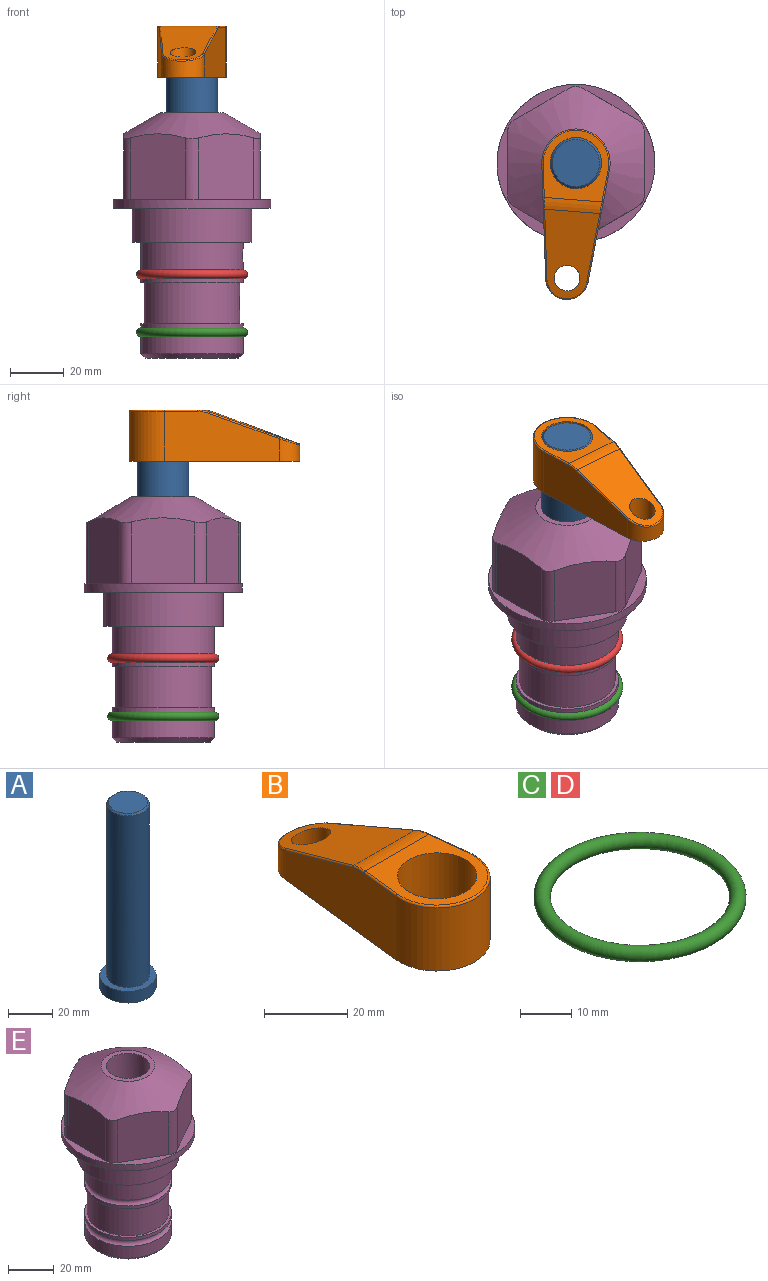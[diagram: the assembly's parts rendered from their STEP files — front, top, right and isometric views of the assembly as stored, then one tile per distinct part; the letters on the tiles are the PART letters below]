
ASSEMBLY  parts=5 mates=3
PART A: 6 faces, bbox 25.4x25.4x101.6 mm
  f0: plane 17.46x17.46mm, normal (0,0,1), area 239.5mm2, adj f5
  f1: plane 25.4x25.4mm, normal (0,0,-1), area 506.7mm2, adj f2
  f2: cylinder r=12.7mm len=25.4mm, axis (0,0,1), area 506.7mm2, adj f1,f3
  f3: plane 25.4x25.4mm, normal (0,0,1), area 221.7mm2, adj f2,f4
  f4: cylinder r=9.53mm len=94.46mm, axis (0,0,1), area 5653mm2, adj f3,f5
  f5: cone r=8.73mm half-angle=45deg, axis (0,0,-1), area 64.4mm2, adj f0,f4
PART B: 44 faces, bbox 27.5x64.5x19.1 mm
  f0: plane 2.3x0.95mm, normal (0,0,-1), area 1mm2, adj f25,f30,f34
  f1: plane 63.5x25.4mm, normal (0,0,-1), area 561.7mm2, adj f2,f3,f4,f5,f6,f7,f19,f20
  f2: cylinder r=12.7mm len=25.4mm, axis (0,0,-1), area 792.2mm2, adj f1,f3,f5,f13
  f3: plane 42.33x18.54mm, normal (0.99,0.11,0), area 647mm2, adj f1,f2,f4,f11,f12,f14
  f4: cylinder r=7.94mm len=15.78mm, axis (0,0,-1), area 158.6mm2, adj f1,f3,f5,f16
  f5: plane 42.33x18.54mm, normal (-0.99,0.11,0), area 647mm2, adj f1,f2,f4,f15,f17,f18
  f6: cylinder r=9.53mm len=19.05mm, axis (0,0,-1), area 1140.1mm2, adj f1,f8
  f7: cylinder r=4.76mm len=10.98mm, axis (0,0,-1), area 276.1mm2, adj f1,f9
  f8: plane 25.83x24.38mm, normal (0,0,1), area 262.2mm2, adj f6,f10,f11,f13,f15
  f9: plane 32.49x20.55mm, normal (0,0.34,0.94), area 489.9mm2, adj f7,f10,f14,f16,f18
  f10: cylinder r=12.7mm len=21.49mm, axis (-1,0,0), area 93.2mm2, adj f8,f9,f12,f17
  f11: cylinder r=0.51mm len=12.34mm, axis (0.11,-0.99,0), area 9.9mm2, adj f3,f8,f12,f13
  f12: bspline ~7.62x1.64mm, area 3.5mm2, adj f3,f10,f11,f14
  f13: torus R=12.19mm, axis (0,0,1), area 33.6mm2, adj f2,f8,f11,f15
  f14: cylinder r=0.51mm len=26.01mm, axis (0.1,-0.93,0.34), area 21.6mm2, adj f3,f9,f12,f16
  f15: cylinder r=0.51mm len=12.34mm, axis (0.11,0.99,0), area 9.9mm2, adj f5,f8,f13,f17
  f16: bspline ~15.78x7.05mm, area 15.7mm2, adj f4,f9,f14,f18
  f17: bspline ~7.62x1.64mm, area 3.5mm2, adj f5,f10,f15,f18
  f18: cylinder r=0.51mm len=26.01mm, axis (0.1,0.93,-0.34), area 21.6mm2, adj f5,f9,f16,f17
  f19: plane 21.6x14.29mm, normal (-0.99,-0.11,0), area 242.6mm2, adj f1,f26,f28,f34,f36,f38
  f20: plane 21.6x14.29mm, normal (0.99,-0.11,0), area 242.6mm2, adj f1,f27,f29,f37,f39,f41
  f21: cylinder r=12.7mm len=14.29mm, axis (0,0,-1), area 173.2mm2, adj f1,f26,f27,f30,f31,f33
  f22: cylinder r=7.94mm len=7.63mm, axis (0,0,-1), area 53.8mm2, adj f1,f28,f29,f42
  f23: plane 2.3x0.95mm, normal (0,0,-1), area 1mm2, adj f25,f33,f37
  f24: plane 17.94x12.32mm, normal (0,-0.34,-0.94), area 191.2mm2, adj f25,f38,f41,f42
  f25: cylinder r=9.53mm len=12.93mm, axis (-1,0,0), area 37.5mm2, adj f0,f23,f24,f31,f36,f39
  f26: cylinder r=1.59mm len=14.29mm, axis (0,0,-1), area 49mm2, adj f1,f19,f21,f32
  f27: cylinder r=1.59mm len=14.29mm, axis (0,0,-1), area 49mm2, adj f1,f20,f21,f35
  f28: cylinder r=1.59mm len=7.28mm, axis (0,0,-1), area 22.1mm2, adj f1,f19,f22,f40
  f29: cylinder r=1.59mm len=7.28mm, axis (0,0,-1), area 22.1mm2, adj f1,f20,f22,f43
  f30: torus R=14.29mm, axis (0,0,1), area 5.8mm2, adj f0,f21,f31,f32
  f31: bspline ~11.06x2.73mm, area 20.8mm2, adj f21,f25,f30,f33
  f32: sphere r=1.59mm, area 5.4mm2, adj f26,f30,f34
  f33: torus R=14.29mm, axis (0,0,1), area 5.8mm2, adj f21,f23,f31,f35
  f34: cylinder r=1.59mm len=1.68mm, axis (-0.11,0.99,0), area 2.4mm2, adj f0,f19,f32,f36
  f35: sphere r=1.59mm, area 5.4mm2, adj f27,f33,f37
  f36: bspline ~5.82x2.33mm, area 7.7mm2, adj f19,f25,f34,f38
  f37: cylinder r=1.59mm len=1.68mm, axis (0.11,0.99,0), area 2.4mm2, adj f20,f23,f35,f39
  f38: cylinder r=1.59mm len=18.33mm, axis (0.1,-0.93,0.34), area 46.7mm2, adj f19,f24,f36,f40
  f39: bspline ~5.82x2.33mm, area 7.7mm2, adj f20,f25,f37,f41
  f40: sphere r=1.59mm, area 3.6mm2, adj f28,f38,f42
  f41: cylinder r=1.59mm len=18.33mm, axis (0.1,0.93,-0.34), area 46.7mm2, adj f20,f24,f39,f43
  f42: bspline ~8.31x1.84mm, area 15.3mm2, adj f22,f24,f40,f43
  f43: sphere r=1.59mm, area 3.6mm2, adj f29,f41,f42
PART C: 1 faces, bbox 44.7x44.7x3.2 mm
  f0: torus R=19.05mm, axis (0,0,1), area 1193.9mm2
PART D: same geometry as C
PART E: 36 faces, bbox 58.7x58.7x91.2 mm
  f0: cylinder r=17.78mm len=35.56mm, axis (0,0,1), area 1670.8mm2, adj f23,f24,f31
  f1: cylinder r=19.05mm len=38.1mm, axis (0,0,1), area 1191.9mm2, adj f26,f27,f30
  f2: plane 58.66x58.66mm, normal (0,0,-1), area 1150.6mm2, adj f3,f28
  f3: cylinder r=29.33mm len=58.66mm, axis (0,0,-1), area 585.1mm2, adj f2,f4
  f4: plane 58.66x58.66mm, normal (0,0,1), area 475.9mm2, adj f3,f5,f6,f7,f8,f9,f10,f11
  f5: plane 24.5x20.32mm, normal (-0.5,0.87,0), area 562.8mm2, adj f4,f15,f16,f17
  f6: plane 24.5x20.32mm, normal (0.5,0.87,0), area 562.8mm2, adj f4,f14,f15,f17
  f7: plane 24.5x23.48mm, normal (1,0,0), area 562.8mm2, adj f4,f13,f14,f17
  f8: plane 24.5x20.32mm, normal (0.5,-0.87,0), area 562.8mm2, adj f4,f12,f13,f17
  f9: plane 24.5x20.32mm, normal (-0.5,-0.87,0), area 562.8mm2, adj f4,f11,f12,f17
  f10: plane 24.5x23.48mm, normal (-1,0,0), area 562.8mm2, adj f4,f11,f16,f17
  f11: cylinder r=5.08mm len=23.01mm, axis (0,0,-1), area 121.2mm2, adj f4,f9,f10,f17
  f12: cylinder r=5.08mm len=23.01mm, axis (0,0,-1), area 121.2mm2, adj f4,f8,f9,f17
  f13: cylinder r=5.08mm len=23.01mm, axis (0,0,-1), area 121.2mm2, adj f4,f7,f8,f17
  f14: cylinder r=5.08mm len=23.01mm, axis (0,0,-1), area 121.2mm2, adj f4,f6,f7,f17
  f15: cylinder r=5.08mm len=23.01mm, axis (0,0,-1), area 121.2mm2, adj f4,f5,f6,f17
  f16: cylinder r=5.08mm len=23.01mm, axis (0,0,-1), area 121.2mm2, adj f4,f5,f10,f17
  f17: cone r=11.73mm half-angle=60deg, axis (0,0,-1), area 2071.8mm2, adj f5,f6,f7,f8,f9,f10,f11,f12
  f18: plane 23.46x23.46mm, normal (0,0,1), area 147.4mm2, adj f17,f35
  f19: plane 34.93x34.93mm, normal (0,0,-1), area 958mm2, adj f29
  f20: cylinder r=19.05mm len=38.1mm, axis (0,0,1), area 760.1mm2, adj f21,f29
  f21: torus R=19.05mm, axis (0,0,1), area 565.3mm2, adj f20,f22
  f22: cylinder r=19.05mm len=38.1mm, axis (0,0,1), area 190mm2, adj f21,f23
  f23: plane 38.1x38.1mm, normal (0,0,1), area 146.9mm2, adj f0,f22
  f24: plane 38.1x38.1mm, normal (0,0,-1), area 146.9mm2, adj f0,f25
  f25: cylinder r=19.05mm len=38.1mm, axis (0,0,1), area 190mm2, adj f24,f26
  f26: torus R=19.05mm, axis (0,0,1), area 565.3mm2, adj f1,f25
  f27: plane 44.45x44.45mm, normal (0,0,-1), area 411.7mm2, adj f1,f28
  f28: cylinder r=22.23mm len=44.45mm, axis (0,0,1), area 1773.5mm2, adj f2,f27
  f29: cone r=19.05mm half-angle=45deg, axis (0,0,1), area 257.5mm2, adj f19,f20
  f30: cylinder r=3.17mm len=6.75mm, axis (-1,0,0), area 128mm2, adj f1,f33
  f31: cylinder r=3.17mm len=6.35mm, axis (-1,0,0), area 102.5mm2, adj f0,f33
  f32: plane 25.4x25.4mm, normal (0,0,1), area 506.7mm2, adj f33
  f33: cylinder r=12.7mm len=66.42mm, axis (0,0,-1), area 5236.2mm2, adj f30,f31,f32,f34
  f34: cone r=9.53mm half-angle=30deg, axis (0,0,-1), area 443.4mm2, adj f33,f35
  f35: cylinder r=9.53mm len=19.05mm, axis (0,0,-1), area 849mm2, adj f18,f34
PLACE A rot(axis=(0,0,-1),94.5deg) t=(0,0,-5.93)mm
PLACE B rot(axis=(0,0,1),175.5deg) t=(0,0,48.68)mm
PLACE C t=(0,0,-21.59)mm
PLACE D at identity
PLACE E at identity fixed
MATE fastened C.f0 <-> E.f0  axis (0,0,1) through (0,0,-46.1)mm
MATE cylindrical A.f2 <-> E.f0  axis (0,0,1) through (0,0,19.7)mm
MATE fastened B.f2 <-> A.f2  axis (0,0,1) through (0,0,67.73)mm
